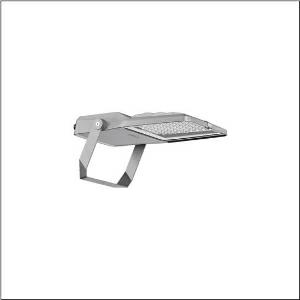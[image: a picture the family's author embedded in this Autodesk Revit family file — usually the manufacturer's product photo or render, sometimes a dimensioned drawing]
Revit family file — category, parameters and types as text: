
# Revit family: floodlight_fl_21_iq_mini___pl61_5xa7772d4c1a_f35a
name_source: partatom
category: Lighting Fixtures
units: mm (PartAtom-declared; Revit-internal decimal feet)

## family parameters
Cut with Voids When Loaded = No
Host = Face
Light Source = No
Part Type = Normal
Room Calculation Point = No
Round Connector Dimension = Use Diameter
Shared = No

## types (1)
- --- (1 x LED, 18260 lm, 143 W, 4000K)
    Apparent Load = 143 VA
    CIE Flux Codes = 33 65 98 100 100
    Color Rendering = 70
    Color Temperature = 4000K
    Default Elevation = 1800 mm
    Description = Floodlight FL 21 iQ mini, floodlight, primary light control with lens, of PMMA, primary optical cover: protective disc, of toughened safety glass, transparent, light distribution: PL61, light emission: direct distribution, installation type: surface-mounted, LED, High Power LED, rated luminous flux: 18.260lm, luminous efficacy: 128lm/W, light colour: 740, colour temperature: 4000K, control gear: iQ Street-Remote/DALI, control: Street-Remote, Auto-Match, Temp-Guard, Night-Set, Smart-Wire, Desk-Remote (wireless, voltage-free reading and setting of iQ features in the workshop via application-optimized NFC function/RFID function), optimised constant luminous flux control (CLO 2.0), with terminal, 6-pole, mains connection: 220..240V, AC, 50/60Hz, start of lifetime: 143W, end of service life: 152W, reduction: 61W, luminaire housing, of diecast aluminium, powder-coated, Siteco® metallic grey (DB 702S), corrosivity category C5 mid according to DIN EN ISO 12944, suitable for swimming pools, chlorine-resistant, sealing non-destructively replaceable, mounting bracket, of steel, galvanised, powder-coated, Siteco® metallic grey (DB 702S), protection rating (complete): IP66, insulation class (complete): insulation class II (safety insulation), certification: CE, ENEC, VDE, protection symbol: D, impact resistance: IK08, permissible operating ambient temperature: -40..+40°C, permissible operating ambient temperature for outdoor applications: -40..+50°C, standard: DIN EN 12944, LABS conformity tested according to VDMA 24364:2018-05, packaging unit: 1 piece

Light Distribution: PL61
    Height = 70 mm
    Lamp = 1 x LED
    Lamp Light Flux = 18260 lm
    Lamp Power = 143 W
    Lamp count = 1
    Length = 485 mm
    Luminous efficacy = 128 lm/W
    Manufacturer = Siteco
    ModVariant = No
    Model = 5XA7772D4C1A
    Number of Poles = 1
    OnlyDefault = Yes
    Power Factor = 1
    Product Name = Floodlight FL 21 iQ mini | PL61
    Product group = floodlight | pylon annexe
    ProductGroupID = 6200
    Protection Class = Protection class II
    Protection Degree = IP 66
    RLX_Detail_Level = 1
    RLX_Emergency_Light_Flux = 0 lm
    RLX_Emergency_Type = 0
    RLX_Emergency_Type_DB = No
    RlxData = <blob elided: 96585 chars, md5=591de83b>
    Socket = socket
    Standby Power = 0 W
    System Light Flux = 18260 lm
    System Power = 143 W
    Type Comments = factory setting: luminous flux: 100 % | dim-lin: 254 | 730 mA
    Type Image = l_1006845.jpg
    URL = http://relux.com
    VarID = @adj_172376
    Voltage = 0 V
    Weight = 0.00 kg
    Width = 337 mm

## geometry (parser evidence)
native form markers: Blend x4, Sweep x11
no freeform markers — native parametric forms only
